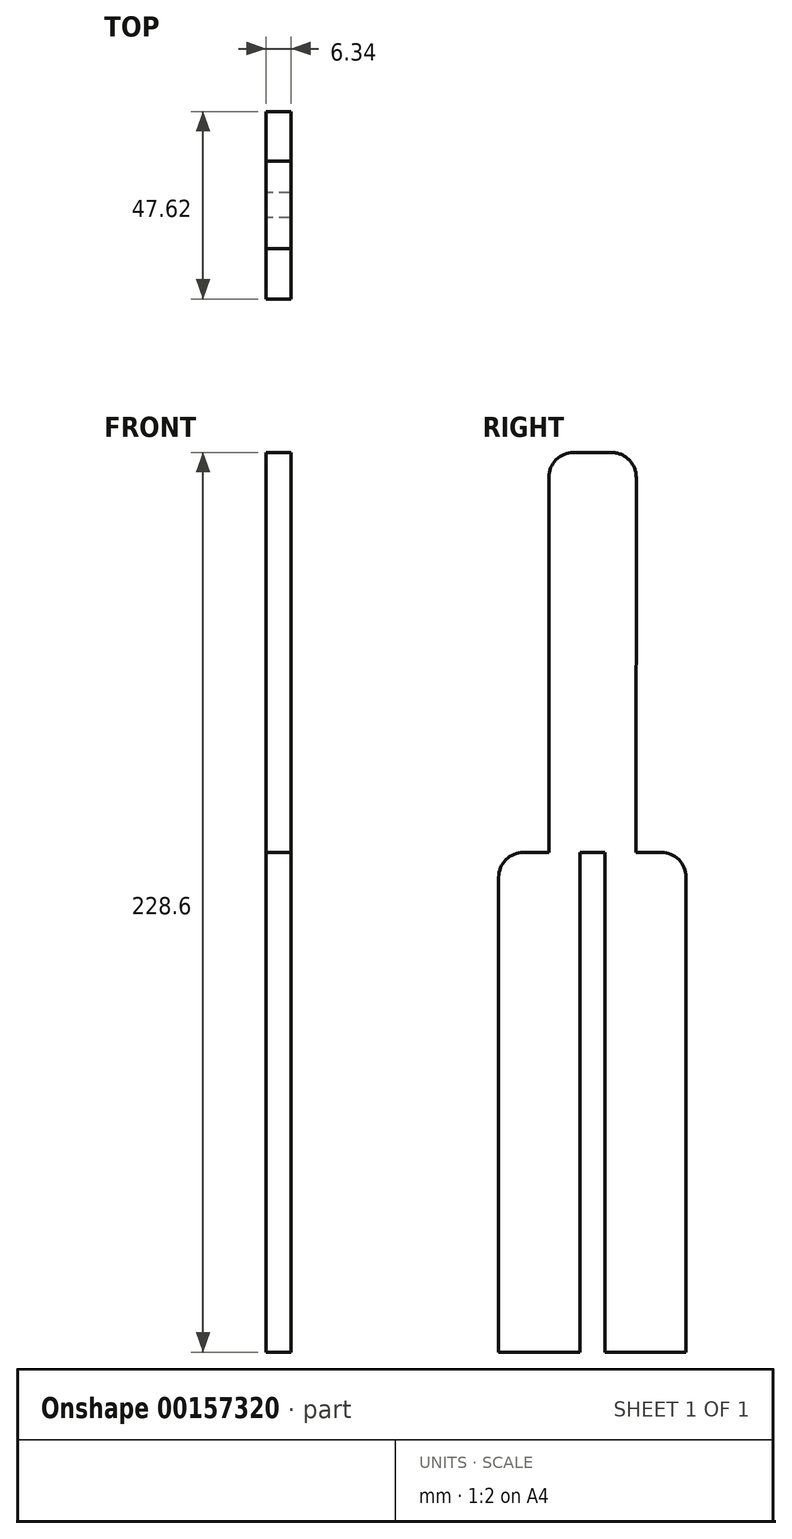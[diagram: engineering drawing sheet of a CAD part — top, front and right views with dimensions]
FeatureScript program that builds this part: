
annotation { "Feature Type Name" : "Feature", "Feature Type Description" : "" }
export const myFeature = defineFeature(function(context is Context, id is Id, definition is map)
    precondition{}
    {
        {
            var Q0;
            Q0=qCreatedBy(makeId("Right.planeOp"),FACE);
            var sketch = newSketch(context, id + "F0", { "sketchPlane" : qUnion([Q0])});
            skLineSegment(sketch, "E0.bottom", {"start": v(23.81, -63.5) * mm, "end": v(3.18, -63.5) * mm});
            skLineSegment(sketch, "E0.top", {"start": v(17.46, 63.5) * mm, "end": v(17.46, 63.5) * mm});
            skLineSegment(sketch, "E0.left", {"start": v(23.81, -63.5) * mm, "end": v(23.81, 57.15) * mm});
            skLineSegment(sketch, "E0.right", {"start": v(-23.81, -63.5) * mm, "end": v(-23.81, 57.15) * mm});
            skPoint(sketch, "E0.middle", {"position": v(0, 0) * mm});
            skLineSegment(sketch, "E1", {"start": v(-11.1, 63.5) * mm, "end": v(-11.1, 158.75) * mm});
            skLineSegment(sketch, "E2", {"start": v(-4.75, 165.1) * mm, "end": v(4.77, 165.1) * mm});
            skLineSegment(sketch, "E3", {"start": v(11.12, 158.75) * mm, "end": v(11.11, 63.5) * mm});
            skLineSegment(sketch, "E4.trimOffspring", {"start": v(-17.45, 63.5) * mm, "end": v(-17.46, 63.5) * mm});
            skPoint(sketch, "E5.start.orphan", {"position": v(0, -63.5) * mm});
            skPoint(sketch, "E6.visualSharp", {"position": v(-11.1, 63.5) * mm});
            skPoint(sketch, "E7.visualSharp", {"position": v(11.11, 63.5) * mm});
            skPoint(sketch, "E8.visualSharp", {"position": v(-23.81, 63.5) * mm});
            skArc(sketch, "E8.filletArc", {"start": v(-17.46, 63.5) * mm, "mid": v(-21.95, 61.64) * mm, "end": v(-23.81, 57.15) * mm});
            skPoint(sketch, "E9.visualSharp", {"position": v(23.81, 63.5) * mm});
            skArc(sketch, "E9.filletArc", {"start": v(23.81, 57.15) * mm, "mid": v(21.95, 61.64) * mm, "end": v(17.46, 63.5) * mm});
            skPoint(sketch, "E10.visualSharp", {"position": v(11.13, 165.1) * mm});
            skArc(sketch, "E10.filletArc", {"start": v(11.12, 158.75) * mm, "mid": v(9.26, 163.24) * mm, "end": v(4.77, 165.1) * mm});
            skPoint(sketch, "E11.visualSharp", {"position": v(-11.1, 165.1) * mm});
            skArc(sketch, "E11.filletArc", {"start": v(-4.75, 165.1) * mm, "mid": v(-9.24, 163.24) * mm, "end": v(-11.1, 158.75) * mm});
            skLineSegment(sketch, "E12", {"start": v(-3.18, -63.5) * mm, "end": v(-3.18, 63.5) * mm});
            skLineSegment(sketch, "E13", {"start": v(-3.18, 63.5) * mm, "end": v(3.17, 63.5) * mm});
            skLineSegment(sketch, "E14", {"start": v(3.17, 63.5) * mm, "end": v(3.17, -63.5) * mm});
            skLineSegment(sketch, "E15.trimOffspring", {"start": v(-3.18, -63.5) * mm, "end": v(-23.81, -63.5) * mm});
            skLineSegment(sketch, "E16", {"start": v(-17.45, 63.5) * mm, "end": v(-11.1, 63.5) * mm});
            skLineSegment(sketch, "E17", {"start": v(11.11, 63.5) * mm, "end": v(17.46, 63.5) * mm});
            skSolve(sketch);
        }
        {
            var Q0;
            Q0=qSketchRegion(id+"F0",true);
            extrude(context, id + "F1", {"entities" : qUnion([Q0]), "endBound" : BoundingType.SYMMETRIC, "depth" : 6.35 * mm});
        }
    });
